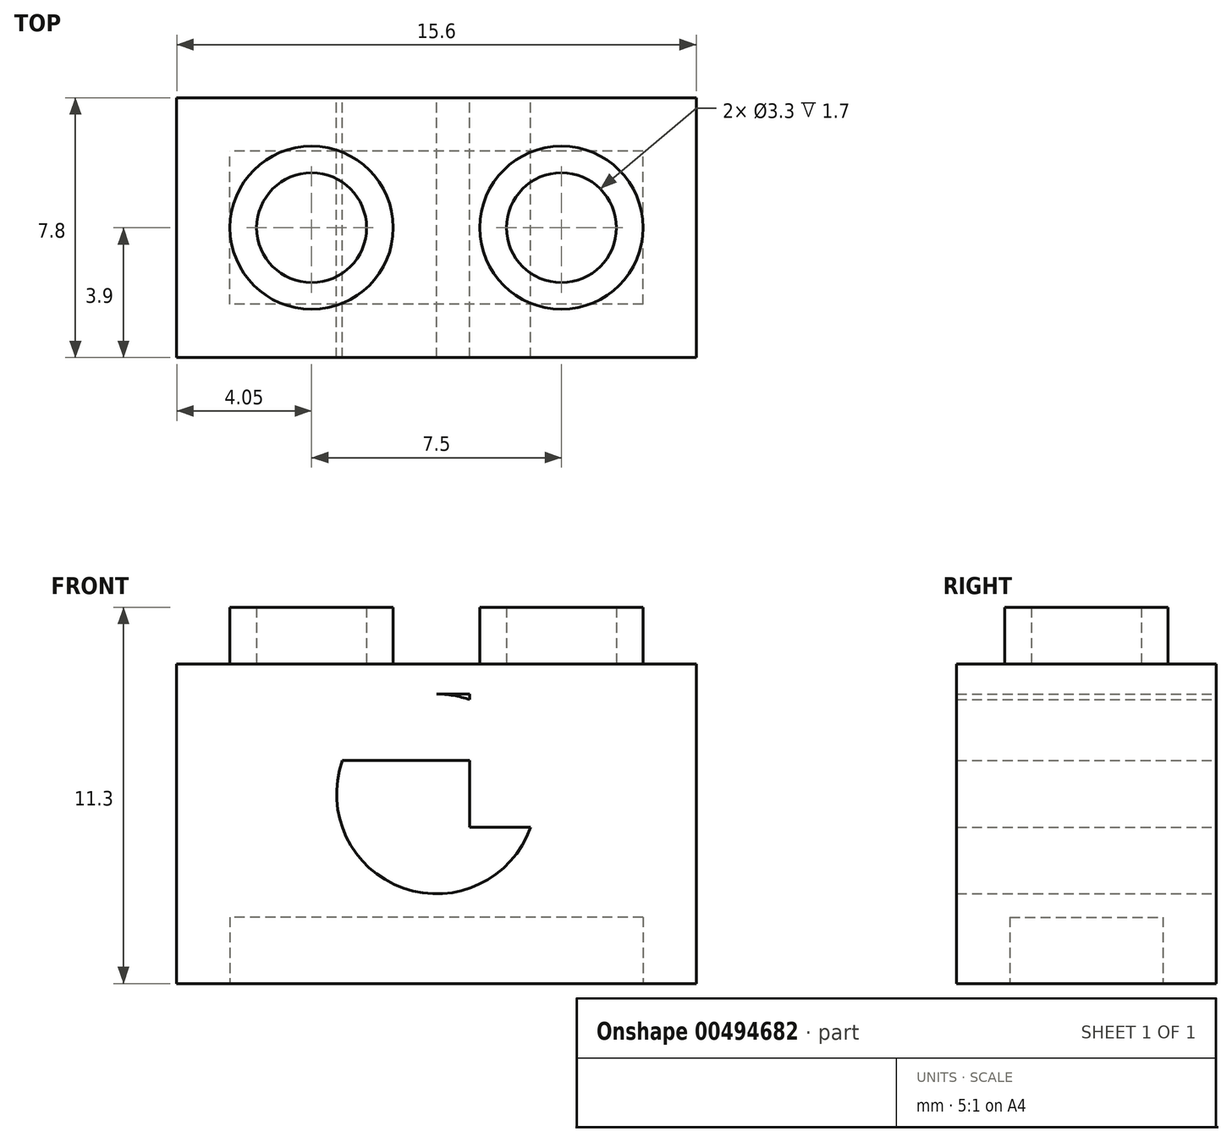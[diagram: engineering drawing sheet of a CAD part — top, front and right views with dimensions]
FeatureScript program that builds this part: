
annotation { "Feature Type Name" : "Feature", "Feature Type Description" : "" }
export const myFeature = defineFeature(function(context is Context, id is Id, definition is map)
    precondition{}
    {
        {
            var Q0;
            Q0=qCreatedBy(makeId("Front.planeOp"),FACE);
            var sketch = newSketch(context, id + "F0", { "sketchPlane" : qUnion([Q0])});
            skLineSegment(sketch, "E0", {"start": v(-0.25, 9.52) * mm, "end": v(-0.25, -0.08) * mm});
            skLineSegment(sketch, "E1", {"start": v(-0.25, -0.08) * mm, "end": v(15.35, -0.08) * mm});
            skLineSegment(sketch, "E2", {"start": v(15.35, -0.08) * mm, "end": v(15.35, 9.52) * mm});
            skLineSegment(sketch, "E3", {"start": v(-0.25, 9.52) * mm, "end": v(15.35, 9.52) * mm});
            skCircle(sketch, "E4", {"center": v(7.55, 5.62) * mm, "radius": 3 * mm});
            skPoint(sketch, "E4.centerSnap0", {"position": v(7.55, -0.08) * mm});
            skLineSegment(sketch, "E5.bottom", {"start": v(8.55, 8.62) * mm, "end": v(6.55, 8.62) * mm});
            skLineSegment(sketch, "E5.top", {"start": v(8.55, 2.62) * mm, "end": v(6.55, 2.62) * mm});
            skLineSegment(sketch, "E5.left", {"start": v(8.55, 8.62) * mm, "end": v(8.55, 2.62) * mm});
            skLineSegment(sketch, "E5.right", {"start": v(6.55, 8.62) * mm, "end": v(6.55, 2.62) * mm});
            skLineSegment(sketch, "E6.bottom", {"start": v(10.55, 6.62) * mm, "end": v(4.55, 6.62) * mm});
            skLineSegment(sketch, "E6.top", {"start": v(10.55, 4.62) * mm, "end": v(4.55, 4.62) * mm});
            skLineSegment(sketch, "E6.left", {"start": v(10.55, 6.62) * mm, "end": v(10.55, 4.62) * mm});
            skLineSegment(sketch, "E6.right", {"start": v(4.55, 6.62) * mm, "end": v(4.55, 4.62) * mm});
            skSolve(sketch);
        }
        {
            var Q0;
            {var subQ0=sQuery(id+"F0.wireOp",EDGE,"E6.left");var subQ1=sQuery(id+"F0.wireOp",EDGE,"E4");var subQ2=makeQuery(id+"F0.imprint","INTERSECT",VERTEX,{"derivedFrom":[subQ1,subQ0]});Q0=makeQuery(id+"F0.imprint","IMPRINT",FACE,{"disambiguationData":[TD([[makeQuery(id+"F0.imprint","IMPRINT",EDGE,{"disambiguationData":[TD([[subQ2,1.0]])],"derivedFrom":subQ1}),-1.0]])]});}
            var Q1;
            {var subQ0=sQuery(id+"F0.wireOp",EDGE,"E6.bottom");var subQ1=sQuery(id+"F0.wireOp",EDGE,"E4");var subQ2=makeQuery(id+"F0.imprint","INTERSECT",VERTEX,{"disambiguationData":[OD(0.0)],"derivedFrom":[subQ1,subQ0]});Q1=makeQuery(id+"F0.imprint","IMPRINT",FACE,{"disambiguationData":[TD([[makeQuery(id+"F0.imprint","IMPRINT",EDGE,{"disambiguationData":[TD([[subQ2,1.0]])],"derivedFrom":subQ1}),-1.0]])]});}
            var Q2;
            {var subQ0=sQuery(id+"F0.wireOp",EDGE,"E5.left");var subQ1=sQuery(id+"F0.wireOp",EDGE,"E4");var subQ2=makeQuery(id+"F0.imprint","INTERSECT",VERTEX,{"disambiguationData":[OD(0.0)],"derivedFrom":[subQ1,subQ0]});Q2=makeQuery(id+"F0.imprint","IMPRINT",FACE,{"disambiguationData":[TD([[makeQuery(id+"F0.imprint","IMPRINT",EDGE,{"disambiguationData":[TD([[subQ2,-1.0]])],"derivedFrom":subQ1}),-1.0]])]});}
            var Q3;
            {var subQ0=sQuery(id+"F0.wireOp",EDGE,"E5.bottom");var subQ1=sQuery(id+"F0.wireOp",EDGE,"E4");var subQ2=makeQuery(id+"F0.imprint","INTERSECT",VERTEX,{"derivedFrom":[subQ1,subQ0]});Q3=makeQuery(id+"F0.imprint","IMPRINT",FACE,{"disambiguationData":[TD([[makeQuery(id+"F0.imprint","IMPRINT",EDGE,{"disambiguationData":[TD([[subQ2,-1.0]])],"derivedFrom":subQ1}),-1.0]])]});}
            var Q4;
            {var subQ0=sQuery(id+"F0.wireOp",EDGE,"E6.bottom");var subQ1=sQuery(id+"F0.wireOp",EDGE,"E4");var subQ2=makeQuery(id+"F0.imprint","INTERSECT",VERTEX,{"disambiguationData":[OD(1.0)],"derivedFrom":[subQ1,subQ0]});Q4=makeQuery(id+"F0.imprint","IMPRINT",FACE,{"disambiguationData":[TD([[makeQuery(id+"F0.imprint","IMPRINT",EDGE,{"disambiguationData":[TD([[subQ2,-1.0]])],"derivedFrom":subQ1}),-1.0]])]});}
            var Q5;
            Q5=makeQuery(id+"F0.imprint","IMPRINT",FACE,{"disambiguationData":[TD([[makeQuery(id+"F0.imprint","IMPRINT",EDGE,{"derivedFrom":sQuery(id+"F0.wireOp",EDGE,"E0")}),1.0]])]});
            var Q6;
            {var subQ0=sQuery(id+"F0.wireOp",EDGE,"E6.right");var subQ1=sQuery(id+"F0.wireOp",EDGE,"E4");var subQ2=makeQuery(id+"F0.imprint","INTERSECT",VERTEX,{"derivedFrom":[subQ1,subQ0]});Q6=makeQuery(id+"F0.imprint","IMPRINT",FACE,{"disambiguationData":[TD([[makeQuery(id+"F0.imprint","IMPRINT",EDGE,{"disambiguationData":[TD([[subQ2,-1.0]])],"derivedFrom":subQ1}),-1.0]])]});}
            var Q7;
            {var subQ0=sQuery(id+"F0.wireOp",EDGE,"E5.right");var subQ1=sQuery(id+"F0.wireOp",EDGE,"E4");var subQ2=makeQuery(id+"F0.imprint","INTERSECT",VERTEX,{"disambiguationData":[OD(1.0)],"derivedFrom":[subQ1,subQ0]});Q7=makeQuery(id+"F0.imprint","IMPRINT",FACE,{"disambiguationData":[TD([[makeQuery(id+"F0.imprint","IMPRINT",EDGE,{"disambiguationData":[TD([[subQ2,-1.0]])],"derivedFrom":subQ1}),-1.0]])]});}
            var Q8;
            {var subQ0=sQuery(id+"F0.wireOp",EDGE,"E5.top");var subQ1=sQuery(id+"F0.wireOp",EDGE,"E4");var subQ2=makeQuery(id+"F0.imprint","INTERSECT",VERTEX,{"derivedFrom":[subQ1,subQ0]});Q8=makeQuery(id+"F0.imprint","IMPRINT",FACE,{"disambiguationData":[TD([[makeQuery(id+"F0.imprint","IMPRINT",EDGE,{"disambiguationData":[TD([[subQ2,-1.0]])],"derivedFrom":subQ1}),-1.0]])]});}
            var Q9;
            {var subQ0=sQuery(id+"F0.wireOp",EDGE,"E5.left");var subQ1=sQuery(id+"F0.wireOp",EDGE,"E4");var subQ2=makeQuery(id+"F0.imprint","INTERSECT",VERTEX,{"disambiguationData":[OD(1.0)],"derivedFrom":[subQ1,subQ0]});Q9=makeQuery(id+"F0.imprint","IMPRINT",FACE,{"disambiguationData":[TD([[makeQuery(id+"F0.imprint","IMPRINT",EDGE,{"disambiguationData":[TD([[subQ2,-1.0]])],"derivedFrom":subQ1}),1.0]])]});}
            var Q10;
            {var subQ0=sQuery(id+"F0.wireOp",EDGE,"E6.bottom");var subQ1=sQuery(id+"F0.wireOp",EDGE,"E4");var subQ2=makeQuery(id+"F0.imprint","INTERSECT",VERTEX,{"disambiguationData":[OD(0.0)],"derivedFrom":[subQ1,subQ0]});Q10=makeQuery(id+"F0.imprint","IMPRINT",FACE,{"disambiguationData":[TD([[makeQuery(id+"F0.imprint","IMPRINT",EDGE,{"disambiguationData":[TD([[subQ2,-1.0]])],"derivedFrom":subQ1}),1.0]])]});}
            var Q11;
            {var subQ0=sQuery(id+"F0.wireOp",EDGE,"E5.right");var subQ1=sQuery(id+"F0.wireOp",EDGE,"E4");var subQ2=makeQuery(id+"F0.imprint","INTERSECT",VERTEX,{"disambiguationData":[OD(0.0)],"derivedFrom":[subQ1,subQ0]});Q11=makeQuery(id+"F0.imprint","IMPRINT",FACE,{"disambiguationData":[TD([[makeQuery(id+"F0.imprint","IMPRINT",EDGE,{"disambiguationData":[TD([[subQ2,-1.0]])],"derivedFrom":subQ1}),1.0]])]});}
            var Q12;
            {var subQ0=sQuery(id+"F0.wireOp",EDGE,"E6.top");var subQ1=sQuery(id+"F0.wireOp",EDGE,"E4");var subQ2=makeQuery(id+"F0.imprint","INTERSECT",VERTEX,{"disambiguationData":[OD(0.0)],"derivedFrom":[subQ1,subQ0]});Q12=makeQuery(id+"F0.imprint","IMPRINT",FACE,{"disambiguationData":[TD([[makeQuery(id+"F0.imprint","IMPRINT",EDGE,{"disambiguationData":[TD([[subQ2,-1.0]])],"derivedFrom":subQ1}),1.0]])]});}
            var Q13;
            Q13=qSketchRegion(id+"F2",true);
            extrude(context, id + "F1", {"entities" : qUnion([Q0, Q1, Q2, Q3, Q4, Q5, Q6, Q7, Q8, Q9, Q10, Q11, Q12, Q13]), "depth" : 7.8 * mm});
        }
        {
            var Q0;
            Q0=makeQuery(id+"F1.opExtrude","SWEPT_FACE",FACE,{"disambiguationData":[OSD([sQuery(id+"F0.wireOp",EDGE,"E3")])]});
            var sketch = newSketch(context, id + "F2", { "sketchPlane" : qUnion([Q0])});
            skCircle(sketch, "E7", {"center": v(3.8, -3.9) * mm, "radius": 2.45 * mm});
            skPoint(sketch, "E7.centerSnap0", {"position": v(-0.25, -3.9) * mm});
            skCircle(sketch, "E8", {"center": v(11.3, -3.9) * mm, "radius": 2.45 * mm});
            skPoint(sketch, "E8.centerSnap0", {"position": v(15.35, -3.9) * mm});
            skLineSegment(sketch, "E9", {"start": v(7.55, 0) * mm, "end": v(7.55, -7.8) * mm});
            skCircle(sketch, "E10", {"center": v(3.8, -3.9) * mm, "radius": 1.65 * mm});
            skCircle(sketch, "E11", {"center": v(11.3, -3.9) * mm, "radius": 1.65 * mm});
            skSolve(sketch);
        }
        {
            var Q0;
            Q0=makeQuery(id+"F2.imprint","IMPRINT",FACE,{"disambiguationData":[TD([[makeQuery(id+"F2.imprint","IMPRINT",EDGE,{"derivedFrom":sQuery(id+"F2.wireOp",EDGE,"E7")}),1.0]])]});
            var Q1;
            Q1=makeQuery(id+"F2.imprint","IMPRINT",FACE,{"disambiguationData":[TD([[makeQuery(id+"F2.imprint","IMPRINT",EDGE,{"derivedFrom":sQuery(id+"F2.wireOp",EDGE,"E8")}),1.0]])]});
            extrude(context, id + "F3", {"entities" : qUnion([Q0, Q1]), "operationType" : NewBodyOperationType.ADD, "depth" : 1.7 * mm});
        }
        {
            var Q0;
            Q0=makeQuery(id+"F1.opExtrude","SWEPT_FACE",FACE,{"disambiguationData":[OSD([sQuery(id+"F0.wireOp",EDGE,"E1")])]});
            var sketch = newSketch(context, id + "F4", { "sketchPlane" : qUnion([Q0])});
            skLineSegment(sketch, "E12", {"start": v(-0.25, 3.9) * mm, "end": v(1.35, 3.9) * mm});
            skLineSegment(sketch, "E13", {"start": v(7.55, 7.8) * mm, "end": v(7.55, 6.2) * mm});
            skLineSegment(sketch, "E14.bottom", {"start": v(13.75, 6.2) * mm, "end": v(1.35, 6.2) * mm});
            skLineSegment(sketch, "E14.top", {"start": v(13.75, 1.6) * mm, "end": v(1.35, 1.6) * mm});
            skLineSegment(sketch, "E14.left", {"start": v(13.75, 6.2) * mm, "end": v(13.75, 1.6) * mm});
            skLineSegment(sketch, "E14.right", {"start": v(1.35, 6.2) * mm, "end": v(1.35, 1.6) * mm});
            skLineSegment(sketch, "E15.trimOffspring", {"start": v(13.75, 3.9) * mm, "end": v(15.35, 3.9) * mm});
            skLineSegment(sketch, "E16.trimOffspring", {"start": v(7.55, 1.6) * mm, "end": v(7.55, 0) * mm});
            skSolve(sketch);
        }
        {
            var Q0;
            {var subQ6=sQuery(id+"F4.wireOp",EDGE,"E14.bottom");var subQ7=makeQuery(id+"F4.imprint","INTERSECT",VERTEX,{"derivedFrom":[sQuery(id+"F4.wireOp",EDGE,"E13"),subQ6]});Q0=makeQuery(id+"F4.imprint","IMPRINT",FACE,{"disambiguationData":[TD([[makeQuery(id+"F4.imprint","IMPRINT",EDGE,{"disambiguationData":[TD([[subQ7,1.0]])],"derivedFrom":subQ6}),1.0]])]});}
            extrude(context, id + "F5", {"entities" : qUnion([Q0]), "operationType" : NewBodyOperationType.REMOVE, "oppositeDirection" : true, "depth" : 2 * mm});
        }
    });
